FCSTD DOCUMENT  (FreeCAD 0.20R29410 (Git))
Label: 60_Keyboard_rev02
License: All rights reserved
LicenseURL: http://en.wikipedia.org/wiki/All_rights_reserved
objects: Sketcher::SketchObject×5
note: 5 computed .brp shape members not serialized (recipe doc carries the construction recipe); baked Part::Feature solids carry a one-line shape summary decoded from their .brp

FEATURE [Sketcher::SketchObject] Sketch  label="TopProfile"
  FullyConstrained = true
  expr: Constraints[23] = .Constraints.WallThickness
  sketch-geometry (22):
    g0: LineSegment StartX=-147 StartY=51 StartZ=0 EndX=-147 EndY=-51 EndZ=0
    g1: LineSegment StartX=-147 StartY=-51 StartZ=0 EndX=147 EndY=-51 EndZ=0
    g2: LineSegment StartX=147 StartY=-51 StartZ=0 EndX=147 EndY=51 EndZ=0
    g3: LineSegment StartX=147 StartY=51 StartZ=0 EndX=-147 EndY=51 EndZ=0
    g4: GeomPoint X=0 Y=0 Z=0
    g5: LineSegment StartX=-142 StartY=46 StartZ=0 EndX=-142 EndY=-46 EndZ=0
    g6: LineSegment StartX=-142 StartY=-46 StartZ=0 EndX=142 EndY=-46 EndZ=0
    g7: LineSegment StartX=142 StartY=-46 StartZ=0 EndX=142 EndY=46 EndZ=0
    g8: LineSegment StartX=142 StartY=46 StartZ=0 EndX=-142 EndY=46 EndZ=0
    g9: GeomPoint X=0 Y=0 Z=0
    g10: LineSegment StartX=-142 StartY=-42 StartZ=0 EndX=-142 EndY=42 EndZ=0
    g11: LineSegment StartX=-138 StartY=46 StartZ=0 EndX=138 EndY=46 EndZ=0
    g12: LineSegment StartX=142 StartY=42 StartZ=0 EndX=142 EndY=-42 EndZ=0
    g13: LineSegment StartX=138 StartY=-46 StartZ=0 EndX=-138 EndY=-46 EndZ=0
    g14: ArcOfCircle CenterX=-138 CenterY=-42 CenterZ=0 NormalX=0 NormalY=0 NormalZ=1 AngleXU=0 Radius=4 StartAngle=3.14159 EndAngle=4.71239
    g15: ArcOfCircle CenterX=-138 CenterY=42 CenterZ=0 NormalX=0 NormalY=0 NormalZ=1 AngleXU=0 Radius=4 StartAngle=1.5708 EndAngle=3.14159
    g16: ArcOfCircle CenterX=138 CenterY=42 CenterZ=0 NormalX=0 NormalY=0 NormalZ=1 AngleXU=0 Radius=4 StartAngle=7.75276e-08 EndAngle=1.5708
    g17: ArcOfCircle CenterX=138 CenterY=-42 CenterZ=0 NormalX=0 NormalY=0 NormalZ=1 AngleXU=0 Radius=4 StartAngle=4.71239 EndAngle=6.28319
    g18: LineSegment StartX=-147 StartY=51 StartZ=0 EndX=147 EndY=51 EndZ=0
    g19: LineSegment StartX=147 StartY=51 StartZ=0 EndX=147 EndY=-51 EndZ=0
    g20: LineSegment StartX=147 StartY=-51 StartZ=0 EndX=-147 EndY=-51 EndZ=0
    g21: LineSegment StartX=-147 StartY=-51 StartZ=0 EndX=-147 EndY=51 EndZ=0
  constraints (58):
    c: Coincident(g0,g1)
    c: Coincident(g1,g2)
    c: Coincident(g2,g3)
    c: Coincident(g3,g0)
    c: Horizontal(g1)
    c: Horizontal(g3)
    c: Vertical(g0)
    c: Vertical(g2)
    c: Symmetric(g1,g0,g4)
    c: Coincident(g4,g-1)
    c: DistanceY(g2,g2) = 102  'WallOuterDepth'
    c: DistanceX(g3,g3) = 294  'WallOuterWidth'
    c: Coincident(g5,g6)
    c: Coincident(g6,g7)
    c: Coincident(g7,g8)
    c: Coincident(g8,g5)
    c: Horizontal(g6)
    c: Horizontal(g8)
    c: Vertical(g5)
    c: Vertical(g7)
    c: Symmetric(g6,g5,g9)
    c: Coincident(g9,g4)
    c: DistanceX(g0,g5) = 5  'WallThickness'
    c: DistanceY(g5,g0) = 5
    c: PointOnObject(g10,g5)
    c: PointOnObject(g11,g8)
    c: PointOnObject(g12,g7)
    c: PointOnObject(g12,g7)
    c: Coincident(g14,g13)
    c: Coincident(g14,g10)
    c: Horizontal(g10,g14)
    c: Vertical(g13,g14)
    c: Diameter(g14) = 8  'WallInnerFillet'
    c: Coincident(g15,g10)
    c: Coincident(g15,g11)
    c: Coincident(g16,g11)
    c: Coincident(g16,g12)
    c: Coincident(g17,g13)
    c: Coincident(g17,g12)
    c: Equal(g14,g15)
    c: Equal(g15,g16)
    c: Equal(g16,g17)
    c: Symmetric(g13,g13,g-2)
    c: Symmetric(g10,g10,g-1)
    c: Symmetric(g11,g13,g-1)
    c: Symmetric(g13,g11,g-1)
    c: Vertical(g13,g17)
    c: Vertical(g11,g16)
    c: Coincident(g18,g19)
    c: Coincident(g19,g20)
    c: Coincident(g20,g21)
    c: Coincident(g21,g18)
    c: Horizontal(g18)
    c: Horizontal(g20)
    c: Vertical(g19)
    c: Vertical(g21)
    c: Coincident(g18,g0)
    c: Coincident(g19,g1)
FEATURE [Sketcher::SketchObject] Sketch001  label="RearProfile"
  ExternalGeometry = -> [Sketch]
  FullyConstrained = true
  Placement = pos=(0,51,0) rot=(0,0.707107,0.707107;3.14159rad)
  sketch-geometry (6):
    g0: LineSegment StartX=-147 StartY=0 StartZ=0 EndX=-147 EndY=-22 EndZ=0
    g1: LineSegment StartX=-147 StartY=-22 StartZ=0 EndX=-135 EndY=-34 EndZ=0
    g2: LineSegment StartX=-135 StartY=-34 StartZ=0 EndX=135 EndY=-34 EndZ=0
    g3: LineSegment StartX=135 StartY=-34 StartZ=0 EndX=147 EndY=-22 EndZ=0
    g4: LineSegment StartX=147 StartY=-22 StartZ=0 EndX=147 EndY=0 EndZ=0
    g5: LineSegment StartX=147 StartY=0 StartZ=0 EndX=-147 EndY=0 EndZ=0
  constraints (15):
    c: Coincident(g0,g-3)
    c: Vertical(g0)
    c: Coincident(g0,g1)
    c: Coincident(g1,g2)
    c: Coincident(g2,g3)
    c: Coincident(g3,g4)
    c: Coincident(g4,g-4)
    c: Coincident(g4,g5)
    c: Coincident(g5,g0)
    c: DistanceY(g0,g0) = 22
    c: DistanceY(g1,g0) = 34
    c: Angle(g1,g0) = 2.35619
    c: Equal(g4,g0)
    c: Vertical(g4)
    c: Symmetric(g1,g2,g-2)
FEATURE [Sketcher::SketchObject] Sketch002  label="FrontProfile"
  ExternalGeometry = -> [Sketch]
  FullyConstrained = true
  Placement = pos=(0,-51,0) rot=(1,0,0;1.5708rad)
  sketch-geometry (4):
    g0: LineSegment StartX=-147 StartY=0 StartZ=0 EndX=147 EndY=0 EndZ=0
    g1: LineSegment StartX=147 StartY=0 StartZ=0 EndX=147 EndY=-18 EndZ=0
    g2: LineSegment StartX=147 StartY=-18 StartZ=0 EndX=-147 EndY=-18 EndZ=0
    g3: LineSegment StartX=-147 StartY=-18 StartZ=0 EndX=-147 EndY=0 EndZ=0
  constraints (10):
    c: Coincident(g0,g1)
    c: Coincident(g1,g2)
    c: Coincident(g2,g3)
    c: Coincident(g3,g0)
    c: Horizontal(g2)
    c: Vertical(g1)
    c: Vertical(g3)
    c: Coincident(g0,g-3)
    c: Coincident(g0,g-4)
    c: DistanceY(g3,g3) = 18
FEATURE [Sketcher::SketchObject] Sketch003  label="SideProfile"
  ExternalGeometry = -> [Sketch,Sketch001,Sketch002]
  FullyConstrained = true
  Placement = pos=(147,0,0) rot=(0.57735,0.57735,0.57735;2.0944rad)
  sketch-geometry (9):
    g0: LineSegment StartX=-51 StartY=0 StartZ=0 EndX=51 EndY=1.27e-14 EndZ=0
    g1: LineSegment StartX=51 StartY=1.27e-14 StartZ=0 EndX=51 EndY=-22 EndZ=0
    g2: LineSegment StartX=51 StartY=-22 StartZ=0 EndX=-51 EndY=-18 EndZ=0
    g3: LineSegment StartX=-51 StartY=-18 StartZ=0 EndX=-51 EndY=0 EndZ=0
    g4: LineSegment StartX=51 StartY=-34 StartZ=0 EndX=51 EndY=-22 EndZ=0
    g5: LineSegment StartX=51 StartY=-34 StartZ=0 EndX=-51 EndY=-34 EndZ=0
    g6: LineSegment StartX=-51 StartY=-34 StartZ=0 EndX=-51 EndY=-18 EndZ=0
    g7: LineSegment StartX=51 StartY=-22 StartZ=0 EndX=39 EndY=-34 EndZ=0
    g8: LineSegment StartX=39 StartY=-34 StartZ=0 EndX=-51 EndY=-18 EndZ=0
  constraints (20):
    c: Coincident(g0,g-3)
    c: Coincident(g0,g-4)
    c: Coincident(g0,g1)
    c: Coincident(g1,g-6)
    c: Coincident(g1,g2)
    c: Coincident(g2,g-5)
    c: Coincident(g2,g3)
    c: Coincident(g3,g0)
    c: Coincident(g4,g-7)
    c: Coincident(g4,g1)
    c: Coincident(g4,g5)
    c: Horizontal(g5)
    c: Coincident(g5,g6)
    c: Coincident(g6,g2)
    c: Vertical(g6)
    c: Coincident(g1,g7)
    c: PointOnObject(g7,g5)
    c: Coincident(g7,g8)
    c: Coincident(g8,g2)
    c: Angle(g7,g4) = 0.785398
FEATURE [Sketcher::SketchObject] Sketch004  label="BottomProfile"
  ExternalGeometry = -> [Sketch002,Sketch003,Sketch001]
  FullyConstrained = true
  Placement = pos=(0,0,-34) rot=(1,0,0;3.14159rad)
  sketch-geometry (6):
    g0: GeomPoint X=135 Y=-39 Z=0
    g1: GeomPoint X=-135 Y=-39 Z=0
    g2: LineSegment StartX=-135 StartY=-39 StartZ=0 EndX=-147 EndY=51 EndZ=0
    g3: LineSegment StartX=-147 StartY=51 StartZ=0 EndX=147 EndY=51 EndZ=0
    g4: LineSegment StartX=147 StartY=51 StartZ=0 EndX=135 EndY=-39 EndZ=0
    g5: LineSegment StartX=135 StartY=-39 StartZ=0 EndX=-135 EndY=-39 EndZ=0
  constraints (11):
    c: Vertical(g-6,g0)
    c: Horizontal(g-5,g0)
    c: Symmetric(g0,g1,g-2)
    c: Coincident(g2,g1)
    c: Coincident(g2,g-3)
    c: Coincident(g2,g3)
    c: Coincident(g3,g-4)
    c: Coincident(g3,g4)
    c: Coincident(g4,g0)
    c: Coincident(g4,g5)
    c: Coincident(g5,g2)
